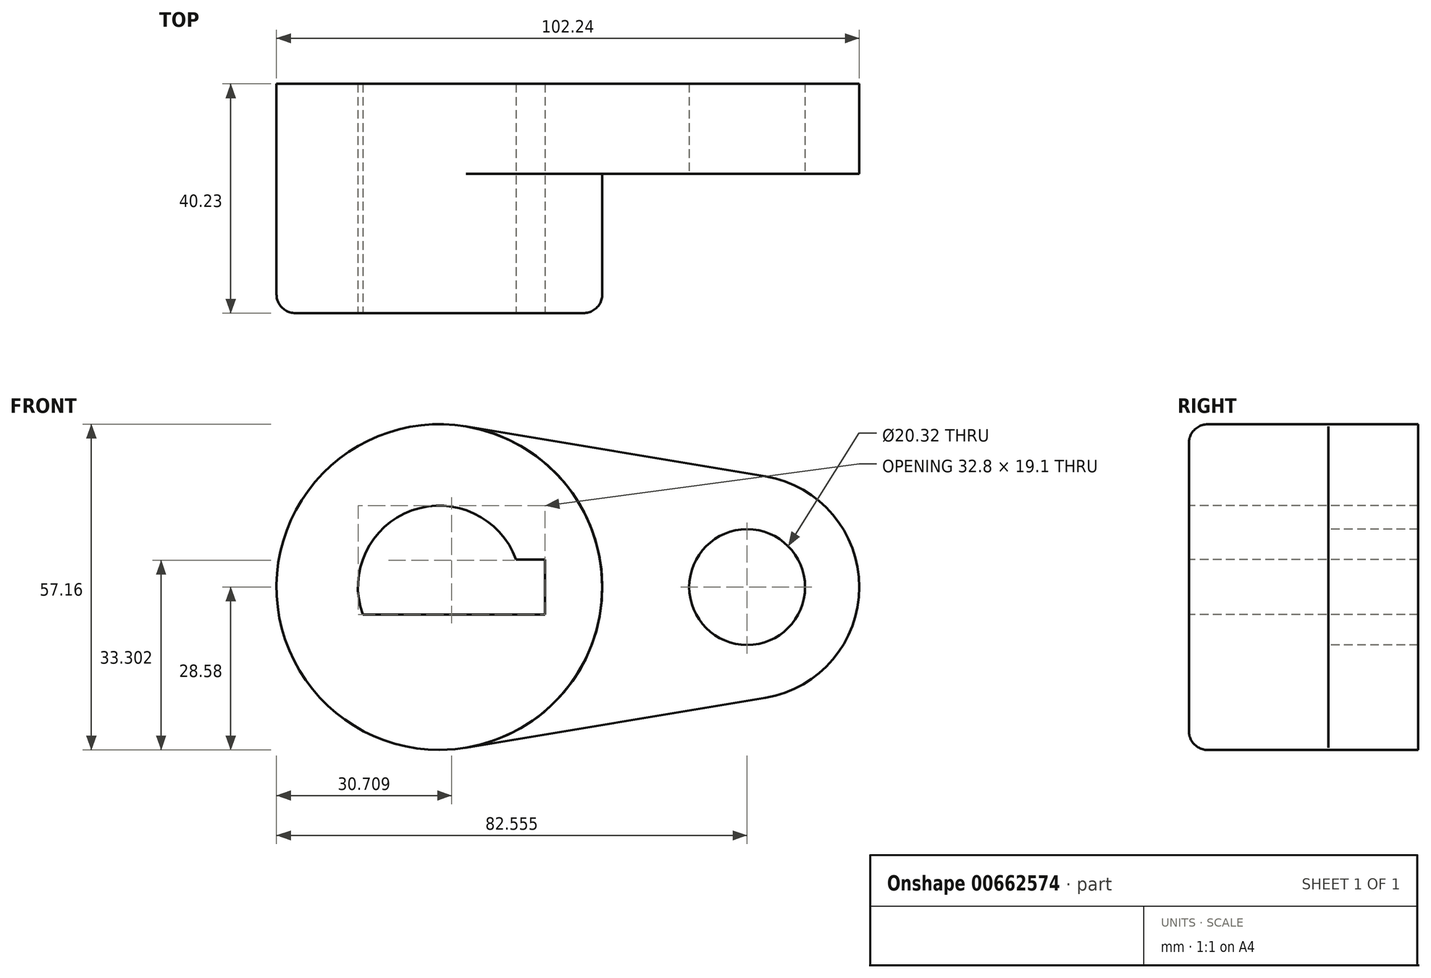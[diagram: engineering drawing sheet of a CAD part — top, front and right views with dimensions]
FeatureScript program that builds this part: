
annotation { "Feature Type Name" : "Feature", "Feature Type Description" : "" }
export const myFeature = defineFeature(function(context is Context, id is Id, definition is map)
    precondition{}
    {
        {
            var Q0;
            Q0=qCreatedBy(makeId("Front.planeOp"),FACE);
            var sketch = newSketch(context, id + "F0", { "sketchPlane" : qUnion([Q0])});
            skCircle(sketch, "E0", {"center": v(0, 0) * mm, "radius": 28.57 * mm});
            skLineSegment(sketch, "E1", {"start": v(4.7, -28.18) * mm, "end": v(57.22, -19.42) * mm});
            skLineSegment(sketch, "E2", {"start": v(4.7, 28.18) * mm, "end": v(57.22, 19.42) * mm});
            skArc(sketch, "E3", {"start": v(57.22, 19.42) * mm, "mid": v(73.66, 0) * mm, "end": v(57.22, -19.42) * mm});
            skSolve(sketch);
        }
        {
            var Q0;
            {var subQ0=sQuery(id+"F0.wireOp",EDGE,"E1");Q0=makeQuery(id+"F0.imprint","IMPRINT",FACE,{"disambiguationData":[TD([[makeQuery(id+"F0.imprint","IMPRINT",EDGE,{"derivedFrom":subQ0}),1.0]])]});}
            extrude(context, id + "F1", {"entities" : qUnion([Q0]), "depth" : 15.77 * mm, "offsetDistance" : 25.4 * mm});
        }
        {
            var Q0;
            Q0=makeQuery(id+"F1.opExtrude","CAP_FACE",FACE,{"disambiguationData":[OSD([sQuery(id+"F0.wireOp",EDGE,"E0"),sQuery(id+"F0.wireOp",EDGE,"E1"),sQuery(id+"F0.wireOp",EDGE,"E2"),sQuery(id+"F0.wireOp",EDGE,"E3")])],"isStart":false});
            var sketch = newSketch(context, id + "F2", { "sketchPlane" : qUnion([Q0])});
            skCircle(sketch, "E4", {"center": v(53.98, 0) * mm, "radius": 10.16 * mm});
            skSolve(sketch);
        }
        {
            var Q0;
            Q0=makeQuery(id+"F2.imprint","IMPRINT",FACE,{"disambiguationData":[TD([[makeQuery(id+"F2.imprint","IMPRINT",EDGE,{"derivedFrom":sQuery(id+"F2.wireOp",EDGE,"E4")}),1.0]])]});
            extrude(context, id + "F3", {"entities" : qUnion([Q0]), "operationType" : NewBodyOperationType.REMOVE, "endBound" : BoundingType.THROUGH_ALL, "oppositeDirection" : true, "depth" : 25.4 * mm, "offsetDistance" : 25.4 * mm});
        }
        {
            var Q0;
            {var subQ0=sQuery(id+"F0.wireOp",EDGE,"E0");var subQ1=makeQuery(id+"F0.imprint","INTERSECT",VERTEX,{"derivedFrom":[subQ0,sQuery(id+"F0.wireOp",EDGE,"E1")]});Q0=makeQuery(id+"F0.imprint","IMPRINT",FACE,{"disambiguationData":[TD([[makeQuery(id+"F0.imprint","IMPRINT",EDGE,{"disambiguationData":[TD([[subQ1,1.0]])],"derivedFrom":subQ0}),1.0]])]});}
            extrude(context, id + "F4", {"entities" : qUnion([Q0]), "operationType" : NewBodyOperationType.ADD, "depth" : 40.23 * mm, "offsetDistance" : 25.4 * mm});
        }
        {
            var Q0;
            Q0=makeQuery(id+"F4.opExtrude","CAP_FACE",FACE,{"disambiguationData":[OSD([sQuery(id+"F0.wireOp",EDGE,"E0")])],"isStart":false});
            var sketch = newSketch(context, id + "F5", { "sketchPlane" : qUnion([Q0])});
            skCircle(sketch, "E5", {"center": v(0, 0) * mm, "radius": 14.29 * mm});
            skLineSegment(sketch, "E6.bottom", {"start": v(18.53, 4.83) * mm, "end": v(-18.53, 4.83) * mm});
            skLineSegment(sketch, "E6.top", {"start": v(18.53, -4.83) * mm, "end": v(-18.53, -4.83) * mm});
            skLineSegment(sketch, "E6.left", {"start": v(18.53, 4.83) * mm, "end": v(18.53, -4.83) * mm});
            skLineSegment(sketch, "E6.right", {"start": v(-18.53, 4.83) * mm, "end": v(-18.53, -4.83) * mm});
            skSolve(sketch);
        }
        {
            var Q0;
            {var subQ0=sQuery(id+"F5.wireOp",EDGE,"E6.bottom");var subQ1=sQuery(id+"F5.wireOp",EDGE,"E5");var subQ2=makeQuery(id+"F5.imprint","INTERSECT",VERTEX,{"disambiguationData":[OD(0.0)],"derivedFrom":[subQ1,subQ0]});Q0=makeQuery(id+"F5.imprint","IMPRINT",FACE,{"disambiguationData":[TD([[makeQuery(id+"F5.imprint","IMPRINT",EDGE,{"disambiguationData":[TD([[subQ2,1.0]])],"derivedFrom":subQ1}),1.0]])]});}
            var Q1;
            {var subQ0=sQuery(id+"F5.wireOp",EDGE,"E6.bottom");var subQ1=sQuery(id+"F5.wireOp",EDGE,"E5");var subQ2=makeQuery(id+"F5.imprint","INTERSECT",VERTEX,{"disambiguationData":[OD(0.0)],"derivedFrom":[subQ1,subQ0]});Q1=makeQuery(id+"F5.imprint","IMPRINT",FACE,{"disambiguationData":[TD([[makeQuery(id+"F5.imprint","IMPRINT",EDGE,{"disambiguationData":[TD([[subQ2,-1.0]])],"derivedFrom":subQ1}),1.0]])]});}
            var Q2;
            {var subQ0=sQuery(id+"F5.wireOp",EDGE,"E6.top");var subQ1=sQuery(id+"F5.wireOp",EDGE,"E5");var subQ2=makeQuery(id+"F5.imprint","INTERSECT",VERTEX,{"disambiguationData":[OD(0.0)],"derivedFrom":[subQ1,subQ0]});Q2=makeQuery(id+"F5.imprint","IMPRINT",FACE,{"disambiguationData":[TD([[makeQuery(id+"F5.imprint","IMPRINT",EDGE,{"disambiguationData":[TD([[subQ2,-1.0]])],"derivedFrom":subQ1}),1.0]])]});}
            var Q3;
            {var subQ5=sQuery(id+"F5.wireOp",EDGE,"E6.left");Q3=makeQuery(id+"F5.imprint","IMPRINT",FACE,{"disambiguationData":[TD([[makeQuery(id+"F5.imprint","IMPRINT",EDGE,{"derivedFrom":subQ5}),-1.0]])]});}
            extrude(context, id + "F6", {"entities" : qUnion([Q0, Q1, Q2, Q3]), "operationType" : NewBodyOperationType.REMOVE, "endBound" : BoundingType.THROUGH_ALL, "oppositeDirection" : true, "depth" : 25.4 * mm, "offsetDistance" : 25.4 * mm});
        }
        {
            var Q0;
            Q0=makeQuery(id+"F4.opExtrude","CAP_EDGE",EDGE,{"disambiguationData":[OSD([sQuery(id+"F0.wireOp",EDGE,"E0")])],"isStart":false});
            fillet(context, id + "F7", {"entities" : qUnion([Q0]), "radius" : 3.3 * mm, "tangentPropagation" : true, "allowEdgeOverflow" : false});
        }
    });
